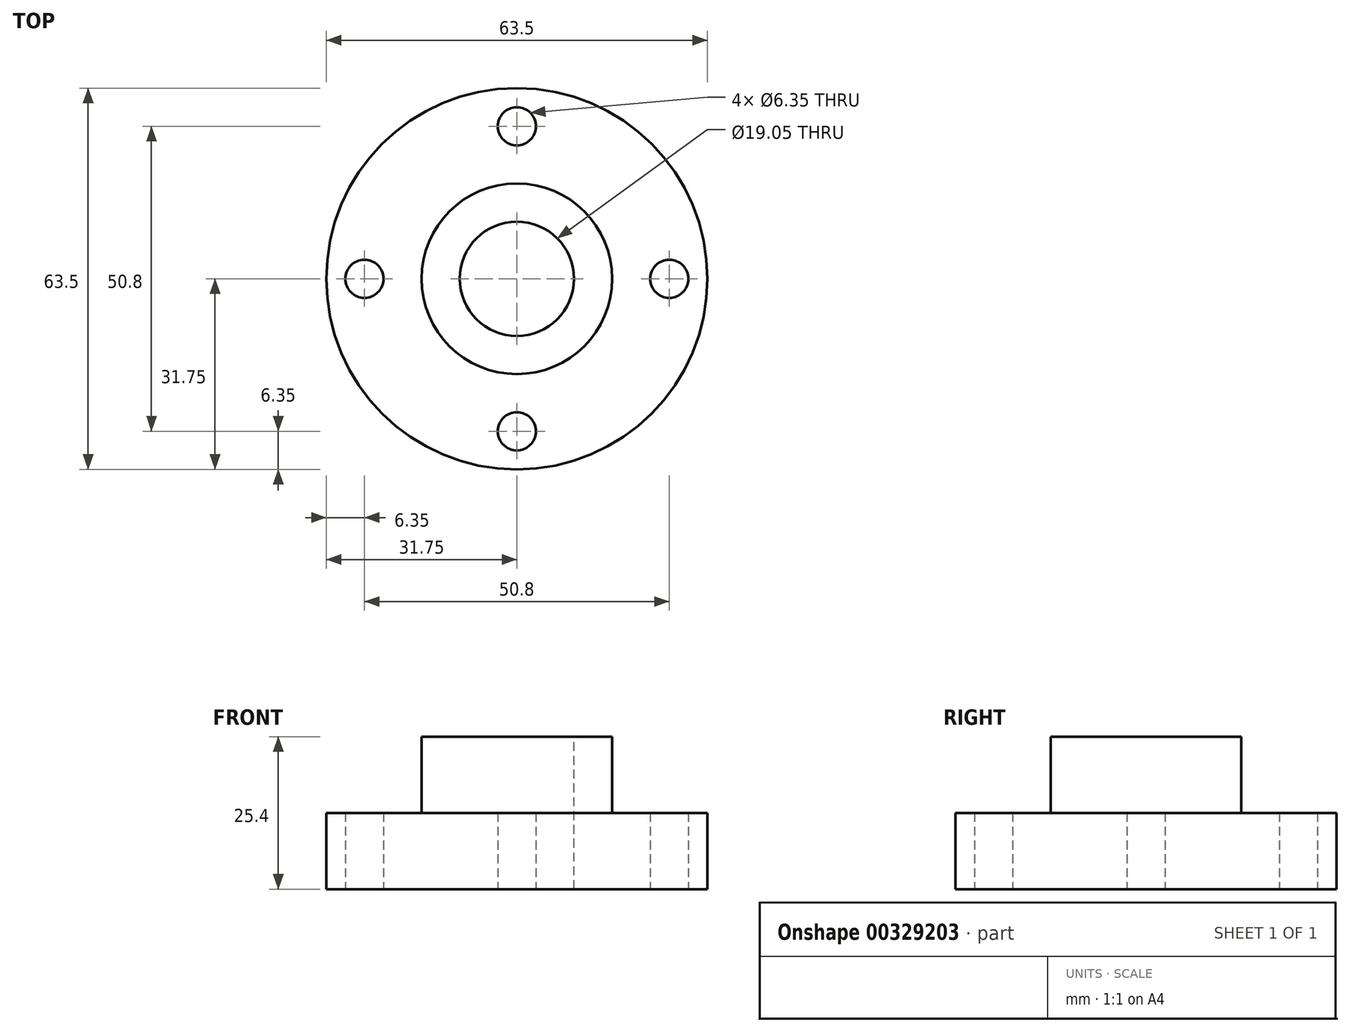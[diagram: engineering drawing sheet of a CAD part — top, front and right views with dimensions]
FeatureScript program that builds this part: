
annotation { "Feature Type Name" : "Feature", "Feature Type Description" : "" }
export const myFeature = defineFeature(function(context is Context, id is Id, definition is map)
    precondition{}
    {
        {
            var Q0;
            Q0=qCreatedBy(makeId("Top.planeOp"),FACE);
            var sketch = newSketch(context, id + "F0", { "sketchPlane" : qUnion([Q0])});
            skCircle(sketch, "E0", {"center": v(0, 0) * mm, "radius": 31.75 * mm});
            skSolve(sketch);
        }
        {
            var Q0;
            Q0 = qSketchRegion(id + "F0", true);
            extrude(context, id + "F1", {"entities" : qUnion([Q0]), "depth" : 12.7 * mm});
        }
        {
            var Q0;
            Q0=makeQuery(id+"F1.opExtrude","CAP_FACE",FACE,{"disambiguationData":[OSD([sQuery(id+"F0.wireOp",EDGE,"E0")])],"isStart":false});
            var sketch = newSketch(context, id + "F2", { "sketchPlane" : qUnion([Q0])});
            skCircle(sketch, "E1", {"center": v(0, 0) * mm, "radius": 15.88 * mm});
            skSolve(sketch);
        }
        {
            var Q0;
            Q0 = qSketchRegion(id + "F2", true);
            extrude(context, id + "F3", {"entities" : qUnion([Q0]), "operationType" : NewBodyOperationType.ADD, "depth" : 12.7 * mm});
        }
        {
            var Q0;
            Q0=qCreatedBy(makeId("Top.planeOp"),FACE);
            var sketch = newSketch(context, id + "F4", { "sketchPlane" : qUnion([Q0])});
            skCircle(sketch, "E2", {"center": v(0, 25.4) * mm, "radius": 3.18 * mm});
            skCircle(sketch, "E3", {"center": v(-25.4, 0) * mm, "radius": 3.18 * mm});
            skCircle(sketch, "E4", {"center": v(25.4, 0) * mm, "radius": 3.18 * mm});
            skCircle(sketch, "E5", {"center": v(0, -25.4) * mm, "radius": 3.18 * mm});
            skSolve(sketch);
        }
        {
            var Q0;
            Q0 = qSketchRegion(id + "F4", true);
            extrude(context, id + "F5", {"entities" : qUnion([Q0]), "operationType" : NewBodyOperationType.REMOVE, "depth" : 25.4 * mm});
        }
        {
            var Q0;
            Q0=makeQuery(id+"F3.opExtrude","CAP_FACE",FACE,{"disambiguationData":[OSD([sQuery(id+"F2.wireOp",EDGE,"E1")])],"isStart":false});
            var sketch = newSketch(context, id + "F6", { "sketchPlane" : qUnion([Q0])});
            skCircle(sketch, "E6", {"center": v(0, 0) * mm, "radius": 9.53 * mm});
            skSolve(sketch);
        }
        {
            var Q0;
            Q0 = qSketchRegion(id + "F6", true);
            extrude(context, id + "F7", {"entities" : qUnion([Q0]), "operationType" : NewBodyOperationType.REMOVE, "endBound" : BoundingType.THROUGH_ALL, "oppositeDirection" : true, "depth" : 25.4 * mm});
        }
    });
